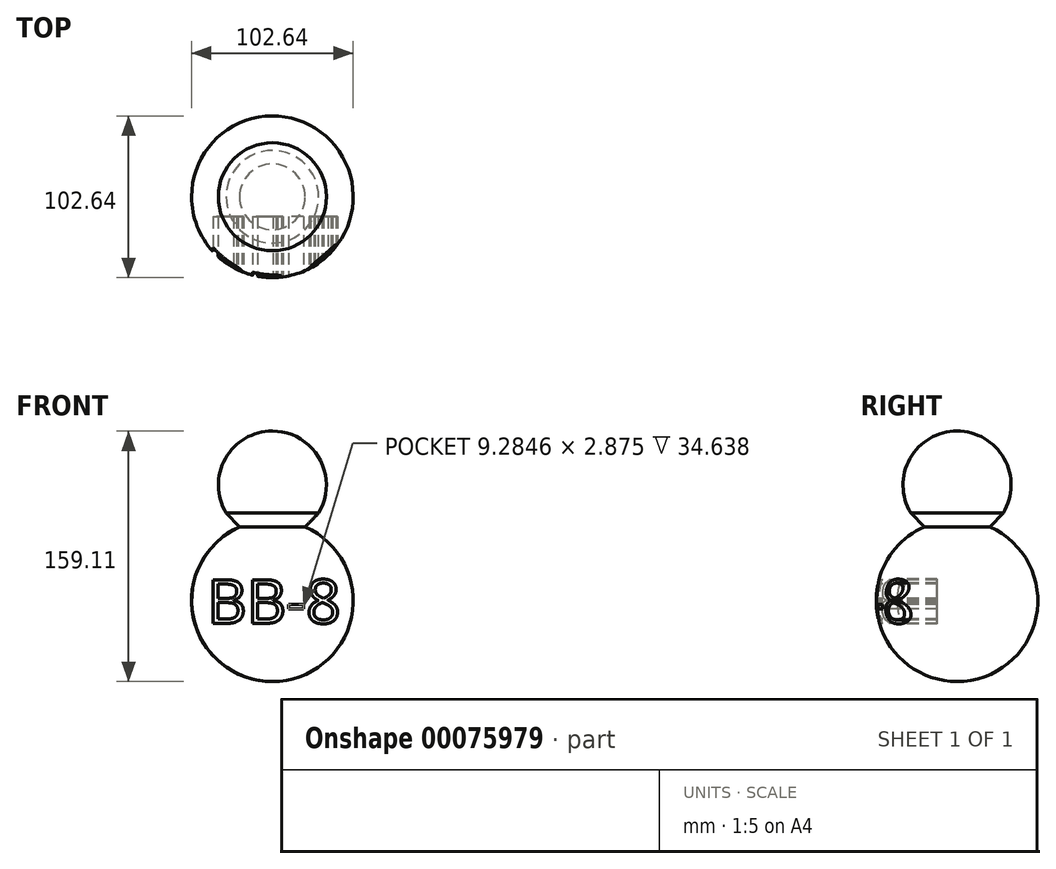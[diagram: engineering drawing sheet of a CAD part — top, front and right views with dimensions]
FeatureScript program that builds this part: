
annotation { "Feature Type Name" : "Feature", "Feature Type Description" : "" }
export const myFeature = defineFeature(function(context is Context, id is Id, definition is map)
    precondition{}
    {
        {
            var Q0;
            Q0=qCreatedBy(makeId("Front.planeOp"),FACE);
            var sketch = newSketch(context, id + "F0", { "sketchPlane" : qUnion([Q0])});
            skArc(sketch, "E0", {"start": v(0, -51.32) * mm, "mid": v(50.2, -10.64) * mm, "end": v(20.82, 46.91) * mm});
            skLineSegment(sketch, "E1", {"start": v(20.82, 46.91) * mm, "end": v(29.38, 55.76) * mm});
            skArc(sketch, "E2", {"start": v(29.38, 55.76) * mm, "mid": v(29.87, 90.35) * mm, "end": v(0, 107.79) * mm});
            skPoint(sketch, "E3.endSnap0", {"position": v(0, 107.79) * mm});
            skLineSegment(sketch, "E4", {"start": v(0, 107.79) * mm, "end": v(0, -51.32) * mm});
            skSolve(sketch);
        }
        {
            var Q0;
            Q0 = qSketchRegion(id + "F0", true);
            var Q1;
            Q1=sQuery(id+"F0.wireOp",EDGE,"E4");
            revolve(context, id + "F1", {"entities" : qUnion([Q0]), "axis" : qUnion([Q1]), "revolveType" : RevolveType.FULL});
        }
        {
            var Q0;
            Q0=qCreatedBy(makeId("Front.planeOp"),FACE);
            cPlane(context, id + "F2", {"entities" : qUnion([Q0]), "cplaneType" : CPlaneType.OFFSET, "offset" : 63.5 * mm, "width" : 152.4 * mm, "height" : 152.4 * mm});
        }
        {
            var Q0;
            Q0=qCreatedBy(id+"F2.planeOp",FACE);
            var sketch = newSketch(context, id + "F3", { "sketchPlane" : qUnion([Q0])});
            skText(sketch, "E5", { "text": "BB-8", "fontName": "OpenSans-Regular.ttf"});
            const initialGuessF3  = {"E5": [-0.0414, -0.01429, 1, 0, 0.02789]};
            skSetInitialGuess(sketch, initialGuessF3);
            skSolve(sketch);
        }
        {
            var Q0;
            Q0 = qSketchRegion(id + "F3", true);
            var Q1;
            Q1=makeQuery(id+"F1.opRevolve","SWEPT_FACE",FACE,{"disambiguationData":[OSD([sQuery(id+"F0.wireOp",EDGE,"E0")])]});
            extrude(context, id + "F4", {"entities" : qUnion([Q0]), "operationType" : NewBodyOperationType.REMOVE, "oppositeDirection" : true, "endBoundEntityFace" : qUnion([Q1]), "depth" : 50.8 * mm});
        }
    });
